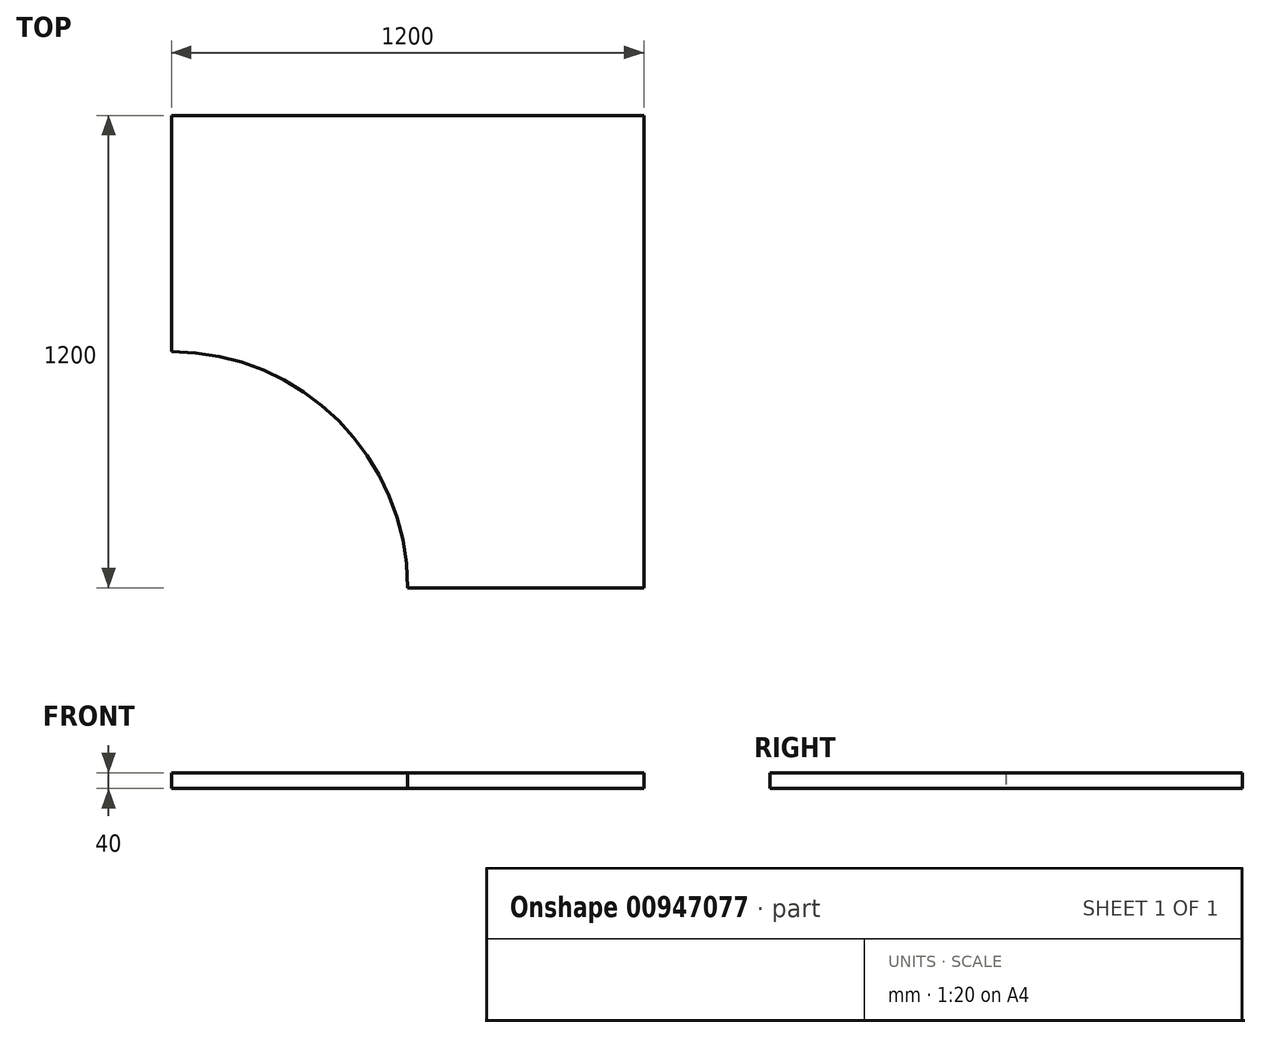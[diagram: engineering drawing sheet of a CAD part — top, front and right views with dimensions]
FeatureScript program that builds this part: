
annotation { "Feature Type Name" : "Feature", "Feature Type Description" : "" }
export const myFeature = defineFeature(function(context is Context, id is Id, definition is map)
    precondition{}
    {
        {
            var Q0;
            Q0=qCreatedBy(makeId("Top.planeOp"),FACE);
            var sketch = newSketch(context, id + "F0", { "sketchPlane" : qUnion([Q0])});
            skLineSegment(sketch, "E0.bottom", {"start": v(600, -600) * mm, "end": v(-600, -600) * mm});
            skLineSegment(sketch, "E0.top", {"start": v(600, 600) * mm, "end": v(-600, 600) * mm});
            skLineSegment(sketch, "E0.left", {"start": v(600, -600) * mm, "end": v(600, 600) * mm});
            skLineSegment(sketch, "E0.right", {"start": v(-600, -600) * mm, "end": v(-600, 600) * mm});
            skPoint(sketch, "E0.middle", {"position": v(0, 0) * mm});
            skPoint(sketch, "E1", {"position": v(-600, 0) * mm});
            skPoint(sketch, "E2", {"position": v(0, -600) * mm});
            skCircle(sketch, "E3", {"center": v(-600, -600) * mm, "radius": 600 * mm});
            skSolve(sketch);
        }
        {
            var Q0;
            {var subQ0=sQuery(id+"F0.wireOp",EDGE,"bFECPbUP-GYgj-6oH5-CII8-n5FEIRWYbGFV");Q0=makeQuery(id+"F0.imprint","IMPRINT",FACE,{"disambiguationData":[TD([[makeQuery(id+"F0.imprint","IMPRINT",EDGE,{"derivedFrom":subQ0}),-1.0]])]});}
            var Q1;
            {var subQ1=sQuery(id+"F0.wireOp",EDGE,"E0.top");Q1=makeQuery(id+"F0.imprint","IMPRINT",FACE,{"disambiguationData":[TD([[makeQuery(id+"F0.imprint","IMPRINT",EDGE,{"derivedFrom":subQ1}),1.0]])]});}
            extrude(context, id + "F1", {"entities" : qUnion([Q0, Q1]), "depth" : 40 * mm, "offsetDistance" : 25 * mm});
        }
    });
